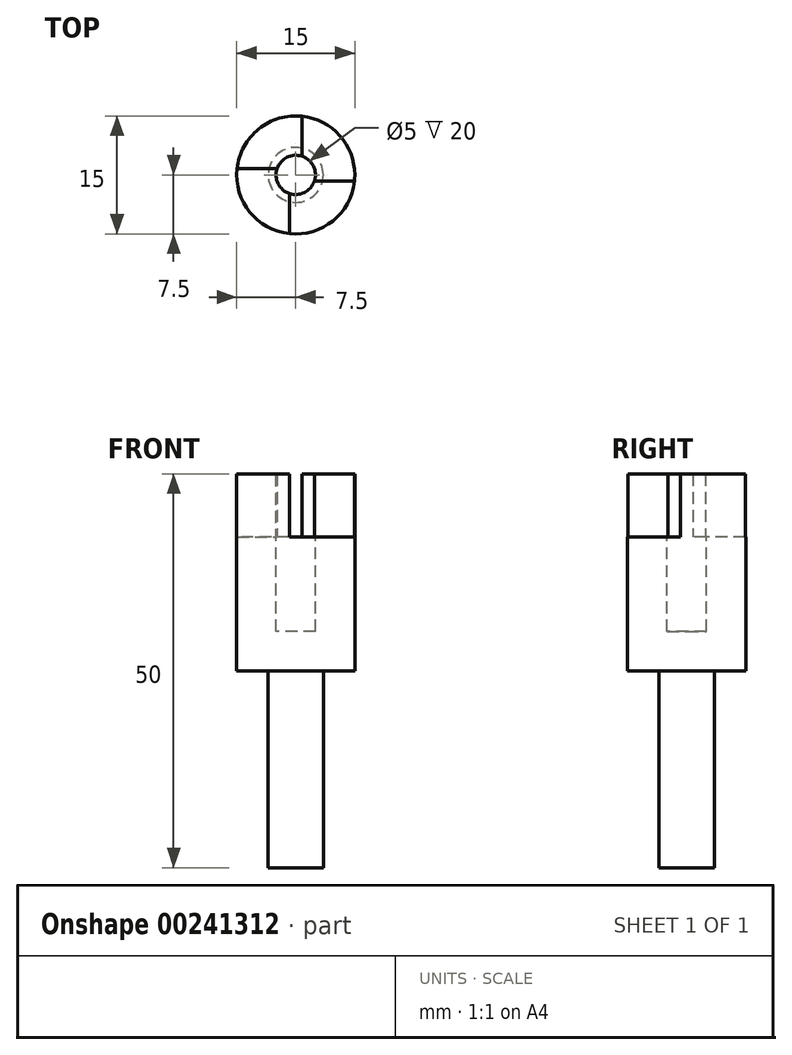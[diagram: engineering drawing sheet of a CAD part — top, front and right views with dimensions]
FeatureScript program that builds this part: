
annotation { "Feature Type Name" : "Feature", "Feature Type Description" : "" }
export const myFeature = defineFeature(function(context is Context, id is Id, definition is map)
    precondition{}
    {
        {
            var Q0;
            Q0=qCreatedBy(makeId("Front.planeOp"),FACE);
            var sketch = newSketch(context, id + "F0", { "sketchPlane" : qUnion([Q0])});
            skLineSegment(sketch, "E0", {"start": v(0, 5) * mm, "end": v(0, -25) * mm});
            skLineSegment(sketch, "E1", {"start": v(7.5, 17) * mm, "end": v(7.5, 0) * mm});
            skLineSegment(sketch, "E2", {"start": v(0, -25) * mm, "end": v(3.5, -25) * mm});
            skLineSegment(sketch, "E3", {"start": v(3.5, -25) * mm, "end": v(3.5, 0) * mm});
            skLineSegment(sketch, "E4", {"start": v(3.5, 0) * mm, "end": v(7.5, 0) * mm});
            skLineSegment(sketch, "E5", {"start": v(0, 5) * mm, "end": v(2.5, 5) * mm});
            skLineSegment(sketch, "E6", {"start": v(2.5, 5) * mm, "end": v(2.5, 17) * mm});
            skPoint(sketch, "E7.orphan", {"position": v(0, 25) * mm});
            skLineSegment(sketch, "E8", {"start": v(2.5, 17) * mm, "end": v(7.5, 17) * mm});
            skSolve(sketch);
        }
        {
            var Q0;
            Q0=makeQuery(id+"F0.imprint","IMPRINT",FACE,{"disambiguationData":[TD([[makeQuery(id+"F0.imprint","IMPRINT",EDGE,{"derivedFrom":sQuery(id+"F0.wireOp",EDGE,"E0")}),1.0]])]});
            var Q1;
            Q1=sQuery(id+"F0.wireOp",EDGE,"E0");
            revolve(context, id + "F1", {"entities" : qUnion([Q0]), "axis" : qUnion([Q1]), "revolveType" : RevolveType.FULL});
        }
        {
            var Q0;
            Q0=makeQuery(id+"F1.opRevolve","SWEPT_FACE",FACE,{"disambiguationData":[OSD([sQuery(id+"F0.wireOp",EDGE,"E8")])]});
            var sketch = newSketch(context, id + "F2", { "sketchPlane" : qUnion([Q0])});
            skLineSegment(sketch, "E9", {"start": v(-7.5, 0.8) * mm, "end": v(-2.37, 0.8) * mm});
            skLineSegment(sketch, "E10", {"start": v(7.5, -0.8) * mm, "end": v(2.37, -0.8) * mm});
            skLineSegment(sketch, "E11", {"start": v(0.8, 7.5) * mm, "end": v(0.8, 2.37) * mm});
            skLineSegment(sketch, "E12", {"start": v(-0.8, -7.5) * mm, "end": v(-0.8, -2.37) * mm});
            skSolve(sketch);
        }
        {
            var Q0;
            {var subQ0=sQuery(id+"F2.wireOp",EDGE,"E10");var subQ1=sQuery(id+"F0.wireOp",EDGE,"E8");var subQ2=makeQuery(id+"F1.opRevolve","SWEPT_EDGE",EDGE,{"disambiguationData":[OSD([sQuery(id+"F0.wireOp",EDGE,"E6"),subQ1])]});var subQ3=makeQuery(id+"F2.imprint","INTERSECT",VERTEX,{"derivedFrom":[subQ2,subQ0]});Q0=makeQuery(id+"F2.imprint","IMPRINT",FACE,{"disambiguationData":[TD([[makeQuery(id+"F2.imprint","IMPRINT",EDGE,{"disambiguationData":[TD([[subQ3,1.0]])],"derivedFrom":subQ0}),-1.0]])]});}
            var Q1;
            {var subQ0=sQuery(id+"F2.wireOp",EDGE,"E9");var subQ1=sQuery(id+"F0.wireOp",EDGE,"E8");var subQ2=makeQuery(id+"F1.opRevolve","SWEPT_EDGE",EDGE,{"disambiguationData":[OSD([sQuery(id+"F0.wireOp",EDGE,"E6"),subQ1])]});var subQ3=makeQuery(id+"F2.imprint","INTERSECT",VERTEX,{"derivedFrom":[subQ2,subQ0]});Q1=makeQuery(id+"F2.imprint","IMPRINT",FACE,{"disambiguationData":[TD([[makeQuery(id+"F2.imprint","IMPRINT",EDGE,{"disambiguationData":[TD([[subQ3,1.0]])],"derivedFrom":subQ0}),-1.0]])]});}
            extrude(context, id + "F3", {"entities" : qUnion([Q0, Q1]), "operationType" : NewBodyOperationType.ADD, "depth" : 8 * mm});
        }
    });
